# Revit family: Faucet-Kitchen-Grohe-LadyLux-30368_Series
name_source: partatom
category: Plumbing Fixtures
revit_build: Autodesk Revit 2014 (Build: 20130308_1515(x64)
units: mm (PartAtom-declared; Revit-internal decimal feet)

## types (2) — shared parameters
ADA Compliant = Yes
Assembly Code = D2020300
CW Connection = Yes
CWFU = 1.5
CalGreen Compliant = Yes
Cold Water Connection Diameter = 3/8"
Default Elevation = 0"
Description = Ladylux Single-Handle Kitchen Faucet
Flow Rate = 1.75 gpm (6.6 L/min)
HW Connection = Yes
HWFU = 1.5
Height = 15 1/4"
Hot Water Connection Diameter = 0"
Installation Type = Deck-Mounted
Length = 7 15/16"
Manufacturer = Grohe
Price = Prices may vary. Please consult Manufacturer Representative for most up-to-date price list.
Shipping Weight = 10.02 lb
URL = https://www.grohe.us
Vent Connection = No
Warranty Documentation Link = https://cdn.cloud.grohe.com
Waste Connection = No
Width = 3 1/4"
cUPC Compliant = Yes
zero-valued in all types: WFU

## per-type parameters (varying)
| type | Finish | Material |
| 30368002 | Brass-Grohe-002-StarLight Chrome | Brass-Grohe-002-StarLight Chrome |
| 30368DC2 | Brass-Grohe-DC2-SuperSteel | Brass-Grohe-DC2-SuperSteel |

note: column(s) folded — value = type name in every type: Model

## geometry (parser evidence)
native form markers: Sweep x1
no freeform markers — native parametric forms only
